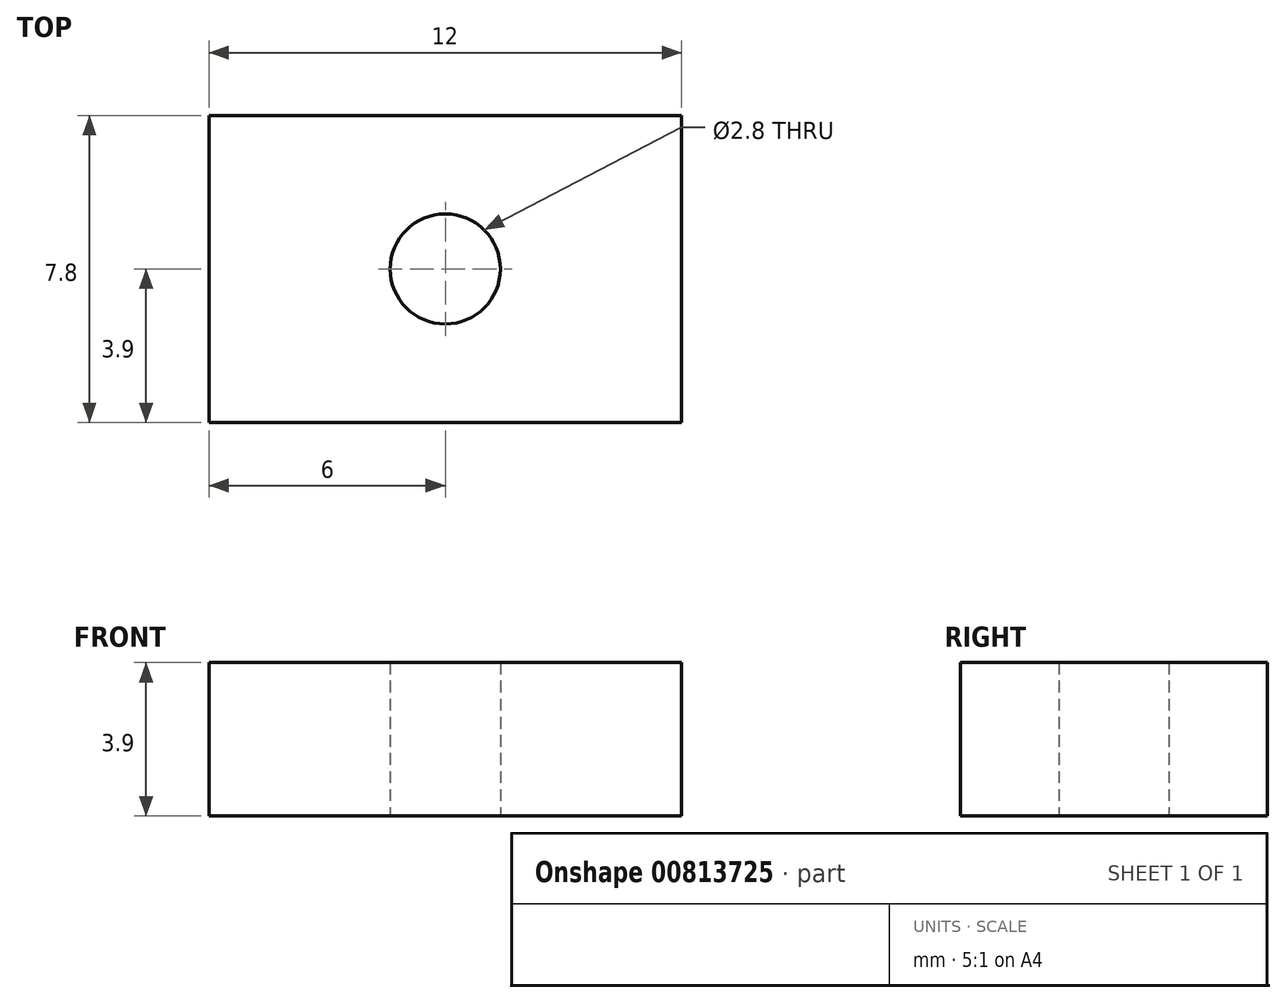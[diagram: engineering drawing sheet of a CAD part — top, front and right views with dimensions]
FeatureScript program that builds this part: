
annotation { "Feature Type Name" : "Feature", "Feature Type Description" : "" }
export const myFeature = defineFeature(function(context is Context, id is Id, definition is map)
    precondition{}
    {
        {
            var Q0;
            Q0=qCreatedBy(makeId("Front.planeOp"),FACE);
            var sketch = newSketch(context, id + "F0", { "sketchPlane" : qUnion([Q0])});
            skLineSegment(sketch, "E0.bottom", {"start": v(-6, 0) * mm, "end": v(0, 0) * mm});
            skLineSegment(sketch, "E0.top", {"start": v(-6, 3.9) * mm, "end": v(0, 3.9) * mm});
            skLineSegment(sketch, "E0.left", {"start": v(-6, 0) * mm, "end": v(-6, 3.9) * mm});
            skLineSegment(sketch, "E1.MirrorCS", {"start": v(6, 3.9) * mm, "end": v(0, 3.9) * mm});
            skLineSegment(sketch, "E2.MirrorCS", {"start": v(6, 0) * mm, "end": v(6, 3.9) * mm});
            skLineSegment(sketch, "E3.MirrorCS", {"start": v(6, 0) * mm, "end": v(0, 0) * mm});
            skSolve(sketch);
        }
        {
            var Q0;
            Q0=qCreatedBy(makeId("Top.planeOp"),FACE);
            var sketch = newSketch(context, id + "F1", { "sketchPlane" : qUnion([Q0])});
            skLineSegment(sketch, "E4", {"start": v(-6, 0) * mm, "end": v(-6, 3.9) * mm});
            skLineSegment(sketch, "E5", {"start": v(-6, 3.9) * mm, "end": v(0, 3.9) * mm});
            skLineSegment(sketch, "E6.MirrorCS", {"start": v(6, 3.9) * mm, "end": v(0, 3.9) * mm});
            skLineSegment(sketch, "E7.MirrorCS", {"start": v(6, 0) * mm, "end": v(6, 3.9) * mm});
            skLineSegment(sketch, "E8.MirrorCS", {"start": v(-6, 0) * mm, "end": v(-6, -3.9) * mm});
            skLineSegment(sketch, "E9.MirrorCS", {"start": v(-6, -3.9) * mm, "end": v(0, -3.9) * mm});
            skLineSegment(sketch, "E10.MirrorCS", {"start": v(6, -3.9) * mm, "end": v(0, -3.9) * mm});
            skLineSegment(sketch, "E11.MirrorCS", {"start": v(6, 0) * mm, "end": v(6, -3.9) * mm});
            skCircle(sketch, "E12", {"center": v(0, 0) * mm, "radius": 1.4 * mm});
            skSolve(sketch);
        }
        {
            var Q0;
            Q0=makeQuery(id+"F1.imprint","IMPRINT",FACE,{"disambiguationData":[TD([[makeQuery(id+"F1.imprint","IMPRINT",EDGE,{"derivedFrom":sQuery(id+"F1.wireOp",EDGE,"E4")}),-1.0]])]});
            extrude(context, id + "F2", {"entities" : qUnion([Q0]), "depth" : 3.9 * mm, "offsetDistance" : 25 * mm});
        }
    });
